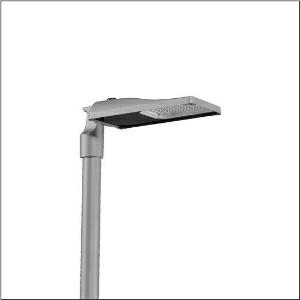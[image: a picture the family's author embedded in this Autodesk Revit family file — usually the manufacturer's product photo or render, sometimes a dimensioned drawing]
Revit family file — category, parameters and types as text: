
# Revit family: streetlight_sl_31_mini___st1_0a_5xh6d3as08ha_e0b1
name_source: partatom
category: Lighting Fixtures
units: mm (PartAtom-declared; Revit-internal decimal feet)

## family parameters
Cut with Voids When Loaded = No
Host = Face
Light Source = No
Part Type = Normal
Room Calculation Point = No
Round Connector Dimension = Use Diameter
Shared = No

## types (1)
- --- (1 x LED, 9230 lm, 68.3 W, 3000K)
    Apparent Load = 68 VA
    CIE Flux Codes = 37 72 97 100 100
    Color Rendering = 70
    Color Temperature = 3000K
    Default Elevation = 1800 mm
    Description = Streetlight SL 31 mini D4i mast luminaire for post-top, side-entry; light control with lens of PMMA; light distribution: ST1.0a, direct asymmetric distribution, for standard-compliant lighting for roads and squares; LED: luminous flux: 9.230lm, light colour: 730, colour temperature: 3000K; luminous efficacy: 135,1lm/W; control: pre-setting: logarithmic dimming characteristic, flexible luminous flux parameterisation, time-dependent luminous flux control, constant luminous flux control, power reduction, intelligent temperature release in ECG and LED module, overheat protection; luminaire housing, of diecast aluminium, SITECO metallic grey (DB 702S), corrosivity category C5 high according to DIN EN ISO 12944; cover of toughened safety glass, transparent, opened without tools; mast flange of diecast aluminium, SITECO metallic grey (DB 702S), spigot size: 76/60mm, mast flange included unmounted; cable length: 8,5m, connection cable pre-assembled; mains connection: 220..240V, AC, 50/60Hz; power consumption (at start of service life): 68,3W / (at end of service life): 74,5W / (with reduced operation 50%): 29,5W; protection rating (complete): IP66; insulation class (complete): insulation class II (safety insulation); impact resistance: IK10; certification: CE, ENEC, ENEC+, VDE, UKCA, ZD4i; permissible operating ambient temperature for outdoor applications: -40..+50°C; packaging unit: 1 piece

Light Distribution: ST1.0a
    Height = 76 mm
    Lamp = 1 x LED
    Lamp Light Flux = 9230 lm
    Lamp Power = 68.3 W
    Lamp count = 1
    Length = 547 mm
    Luminous efficacy = 135 lm/W
    Manufacturer = Siteco
    ModVariant = No
    Model = 5XH6D3AS08HA
    Number of Poles = 1
    OnlyDefault = Yes
    Power Factor = 1
    Product Name = Streetlight SL 31 mini | ST1.0a
    Product group = mast luminaire | pylon top
    ProductGroupID = 6100
    Protection Class = Protection class II
    Protection Degree = IP 66
    RLX_Detail_Level = 1
    RLX_Emergency_Light_Flux = 0 lm
    RLX_Emergency_Type = 0
    RLX_Emergency_Type_DB = No
    RlxData = <blob elided: 24173 chars, md5=39ea0faf>
    Socket = socket
    Standby Power = 0 W
    System Light Flux = 9230 lm
    System Power = 68 W
    Type Comments = factory setting: luminous flux: 100 % | dim-lin: 254 | 692 mA
    Type Image = l_1300330.jpg
    URL = http://relux.com
    VarID = @adj_020321
    Voltage = 0 V
    Weight = 0.00 kg
    Width = 265 mm

## geometry (parser evidence)
native form markers: Blend x4, Sweep x13
no freeform markers — native parametric forms only
